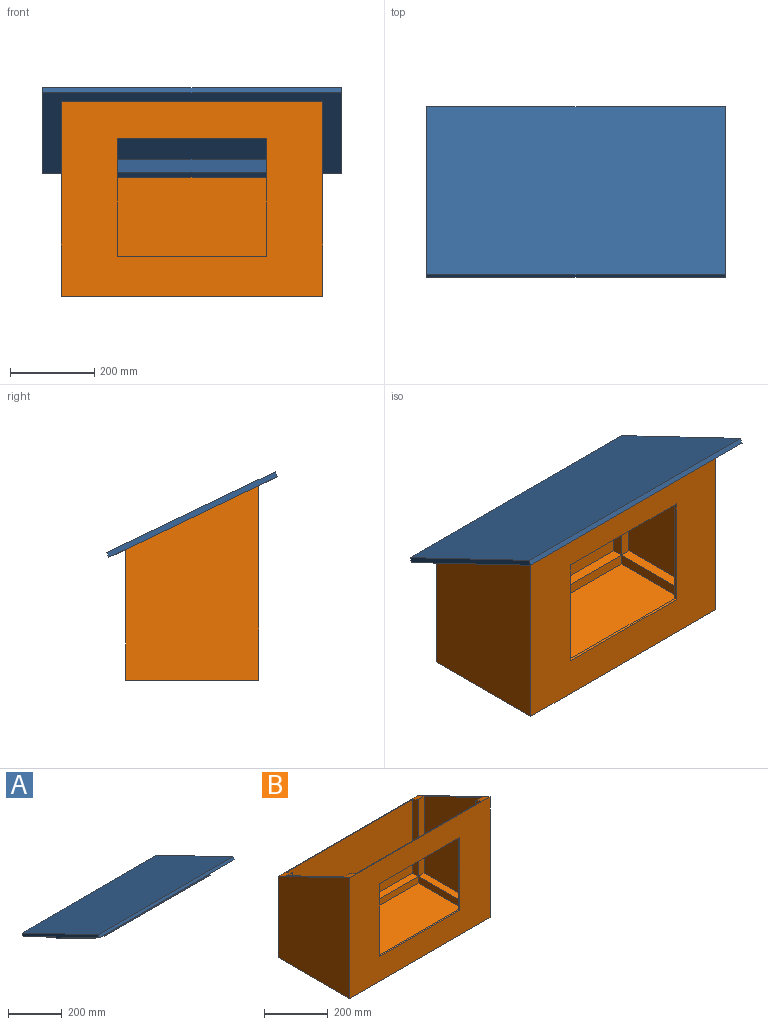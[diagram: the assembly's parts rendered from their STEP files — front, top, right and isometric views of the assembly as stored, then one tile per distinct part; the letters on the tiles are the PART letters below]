
ASSEMBLY  parts=2 mates=1
PART A: 28 faces, bbox 711.2x406.2x213.3 mm
  f0: plane 533.4x31.5mm, normal (0,-1,0), area 16800mm2, adj f1,f7,f8,f27
  f1: cylinder r=12.7mm len=37.59mm, axis (0,0,-1), area 628.3mm2, adj f0,f2,f8,f27
  f2: plane 228.6x141.22mm, normal (1,0,0), area 7200mm2, adj f1,f3,f8,f27
  f3: cylinder r=12.7mm len=37.59mm, axis (0,0,-1), area 628.3mm2, adj f2,f4,f8,f27
  f4: plane 533.4x31.5mm, normal (0,1,0), area 16800mm2, adj f3,f5,f8,f27
  f5: cylinder r=12.7mm len=37.59mm, axis (0,0,-1), area 628.3mm2, adj f4,f6,f8,f27
  f6: plane 228.6x141.22mm, normal (-1,0,0), area 7200mm2, adj f5,f7,f8,f27
  f7: cylinder r=12.7mm len=37.59mm, axis (0,0,-1), area 628.3mm2, adj f0,f6,f8,f27
  f8: plane 609.6x304.8mm, normal (0,-0.43,-0.9), area 45954.1mm2, adj f0,f1,f2,f3,f4,f5,f6,f7
  f9: plane 254x153.42mm, normal (-1,0,0), area 8000mm2, adj f8,f12,f13,f21
  f10: plane 254x153.42mm, normal (1,0,0), area 8000mm2, adj f8,f17,f18,f21
  f11: plane 558.8x31.5mm, normal (0,1,0), area 17600mm2, adj f8,f19,f20,f21
  f12: plane 31.5x25.4mm, normal (0,1,0), area 800mm2, adj f8,f9,f20,f21
  f13: plane 31.5x25.4mm, normal (0,-1,0), area 800mm2, adj f8,f9,f14,f21
  f14: plane 43.69x25.4mm, normal (-1,0,0), area 800mm2, adj f8,f13,f15,f21
  f15: plane 558.8x31.5mm, normal (0,-1,0), area 17600mm2, adj f8,f14,f16,f21
  f16: plane 43.69x25.4mm, normal (1,0,0), area 800mm2, adj f8,f15,f17,f21
  f17: plane 31.5x25.4mm, normal (0,-1,0), area 800mm2, adj f8,f10,f16,f21
  f18: plane 31.5x25.4mm, normal (0,1,0), area 800mm2, adj f8,f10,f19,f21
  f19: plane 43.69x25.4mm, normal (1,0,0), area 800mm2, adj f8,f11,f18,f21
  f20: plane 43.69x25.4mm, normal (-1,0,0), area 800mm2, adj f8,f11,f12,f21
  f21: plane 711.2x400.73mm, normal (0,-0.43,-0.9), area 112888.5mm2, adj f9,f10,f11,f12,f13,f14,f15,f16
  f22: plane 711.2x400.73mm, normal (0,0.43,0.9), area 316128.4mm2, adj f23,f24,f25,f26
  f23: plane 711.2x11.45mm, normal (0,0.9,-0.43), area 9032.2mm2, adj f21,f22,f24,f26
  f24: plane 406.22x203.8mm, normal (1,0,0), area 5645.2mm2, adj f21,f22,f23,f25
  f25: plane 711.2x11.45mm, normal (0,-0.9,0.43), area 9032.2mm2, adj f21,f22,f24,f26
  f26: plane 406.22x203.8mm, normal (-1,0,0), area 5645.2mm2, adj f21,f22,f23,f25
  f27: plane 558.8x254mm, normal (0,-0.43,-0.9), area 157285.8mm2, adj f0,f1,f2,f3,f4,f5,f6,f7
PART B: 31 faces, bbox 622.3x317.5x463.6 mm
  f0: plane 558.8x25.4mm, normal (0,0,1), area 14193.5mm2, adj f14,f15,f16,f26
  f1: plane 254x25.4mm, normal (0,0,1), area 6451.6mm2, adj f6,f7,f8,f27
  f2: plane 254x25.4mm, normal (0,0,1), area 6451.6mm2, adj f11,f12,f13,f29
  f3: plane 622.3x311.15mm, normal (0,1,0), area 193628.6mm2, adj f5,f18,f19,f25
  f4: plane 558.8x428.75mm, normal (0,1,0), area 140232mm2, adj f9,f10,f20,f21,f22,f23,f24,f25
  f5: plane 463.55x317.5mm, normal (-1,0,0), area 122983.6mm2, adj f3,f17,f19,f25
  f6: plane 294.64x25.4mm, normal (0,-1,0), area 7483.9mm2, adj f1,f7,f16,f25
  f7: plane 416.56x254mm, normal (1,0,0), area 90322.4mm2, adj f1,f6,f8,f25
  f8: plane 416.56x25.4mm, normal (0,1,0), area 10580.6mm2, adj f1,f7,f9,f25
  f9: plane 428.75x25.4mm, normal (1,0,0), area 10735.5mm2, adj f4,f8,f20,f25
  f10: plane 428.75x25.4mm, normal (-1,0,0), area 10735.5mm2, adj f4,f11,f20,f25
  f11: plane 416.56x25.4mm, normal (0,1,0), area 10580.6mm2, adj f2,f10,f12,f25
  f12: plane 416.56x254mm, normal (-1,0,0), area 90322.4mm2, adj f2,f11,f13,f25
  f13: plane 294.64x25.4mm, normal (0,-1,0), area 7483.9mm2, adj f2,f12,f14,f25
  f14: plane 294.64x25.4mm, normal (-1,0,0), area 7329mm2, adj f0,f13,f15,f25
  f15: plane 558.8x282.45mm, normal (0,-1,0), area 157831.9mm2, adj f0,f14,f16,f25
  f16: plane 294.64x25.4mm, normal (1,0,0), area 7329mm2, adj f0,f6,f15,f25
  f17: plane 622.3x463.55mm, normal (0,-1,0), area 189112.5mm2, adj f5,f18,f19,f21,f22,f23,f24,f25
  f18: plane 463.55x317.5mm, normal (1,0,0), area 122983.6mm2, adj f3,f17,f19,f25
  f19: plane 622.3x317.5mm, normal (0,0,-1), area 197580.2mm2, adj f3,f5,f17,f18
  f20: plane 558.8x25.4mm, normal (0,0,1), area 14193.5mm2, adj f4,f9,f10,f28
  f21: plane 355.6x6.35mm, normal (0,0,-1), area 2258.1mm2, adj f4,f17,f22,f24
  f22: plane 279.4x6.35mm, normal (1,0,0), area 1774.2mm2, adj f4,f17,f21,f23
  f23: plane 355.6x6.35mm, normal (0,0,1), area 2258.1mm2, adj f4,f17,f22,f24
  f24: plane 279.4x6.35mm, normal (-1,0,0), area 1774.2mm2, adj f4,f17,f21,f23
  f25: plane 622.3x317.5mm, normal (0,0.43,0.9), area 15922.8mm2, adj f3,f4,f5,f6,f7,f8,f9,f10
  f26: plane 558.8x25.4mm, normal (0,-1,0), area 14193.5mm2, adj f0,f27,f29,f30
  f27: plane 254x25.4mm, normal (1,0,0), area 6451.6mm2, adj f1,f26,f28,f30
  f28: plane 558.8x25.4mm, normal (0,1,0), area 14193.5mm2, adj f20,f27,f29,f30
  f29: plane 254x25.4mm, normal (-1,0,0), area 6451.6mm2, adj f2,f26,f28,f30
  f30: plane 558.8x254mm, normal (0,0,1), area 141935.2mm2, adj f26,f27,f28,f29
PLACE A t=(-58.68,32.56,245.45)mm
PLACE B t=(-65.03,26.21,-37.26)mm fixed
MATE fastened A.f15 <-> B.f4  axis (0,-1,0) through (-33.28,32.56,423.25)mm
